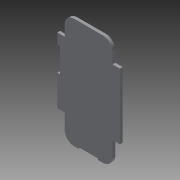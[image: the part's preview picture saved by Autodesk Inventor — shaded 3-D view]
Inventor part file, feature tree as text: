
AUTODESK INVENTOR PART (.ipt)
format: ipt  version: 2015 (Build 190159000, 159)  size: 110,592 bytes
history: native  units: mm
features: extrude x1, fillet x1, sketch x1
ambient origin geometry x8: Origin, YZ Plane, XZ Plane, XY Plane, X Axis, Y Axis, Z Axis, Center Point
bodies: Solid1 (feature_tree)
feature tree (3):
  extrude  "Extrusion1"  Depth=15.4mm
  fillet  "Fillet1"  Radius=15.4mm
  sketch  "Sketch1"  dims[d3=51.0mm d5=15.4mm d8=15.4mm d10=42.2mm d11=28.4mm d13=30.0mm d14=3.0mm d15=40.8mm d16=22.3mm d17=6.0mm d18=50.0mm d19=6.0mm d20=0.0mm d21=20.0mm]
